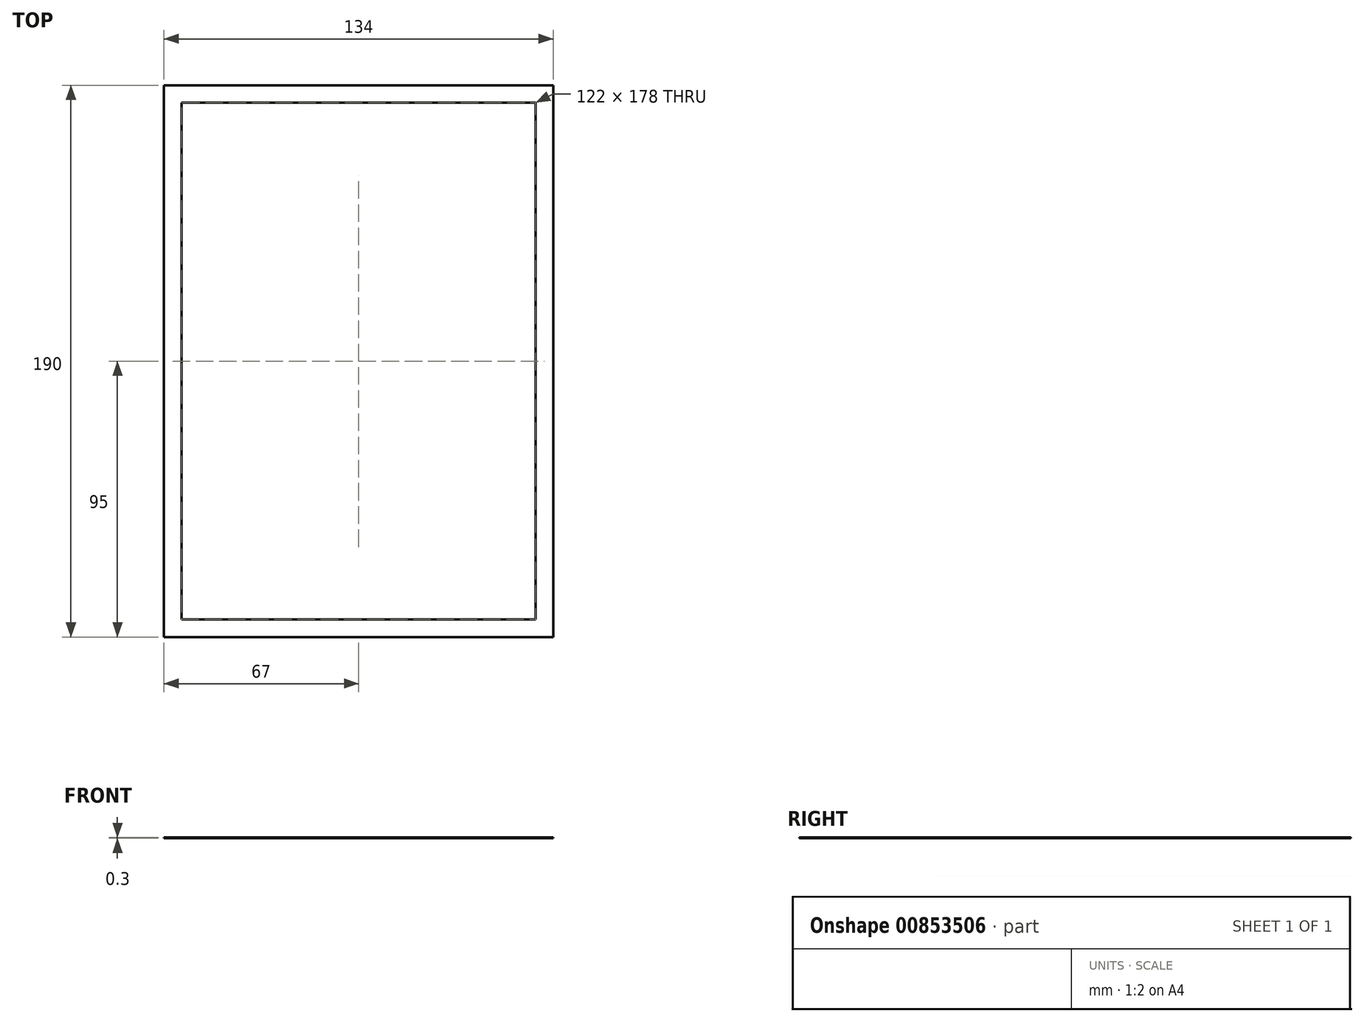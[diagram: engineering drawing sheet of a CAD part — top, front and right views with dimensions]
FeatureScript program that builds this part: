
annotation { "Feature Type Name" : "Feature", "Feature Type Description" : "" }
export const myFeature = defineFeature(function(context is Context, id is Id, definition is map)
    precondition{}
    {
        {
            var Q0;
            Q0=qCreatedBy(makeId("Top.planeOp"),FACE);
            var sketch = newSketch(context, id + "F0", { "sketchPlane" : qUnion([Q0])});
            skLineSegment(sketch, "E0.bottom", {"start": v(-67, 95) * mm, "end": v(67, 95) * mm});
            skLineSegment(sketch, "E0.top", {"start": v(-67, -95) * mm, "end": v(67, -95) * mm});
            skLineSegment(sketch, "E0.left", {"start": v(-67, 95) * mm, "end": v(-67, -95) * mm});
            skLineSegment(sketch, "E0.right", {"start": v(67, 95) * mm, "end": v(67, -95) * mm});
            skPoint(sketch, "E0.middle", {"position": v(0, 0) * mm});
            skLineSegment(sketch, "E1.0", {"start": v(-61, 89) * mm, "end": v(61, 89) * mm});
            skLineSegment(sketch, "E1.1", {"start": v(-61, 89) * mm, "end": v(-61, -89) * mm});
            skLineSegment(sketch, "E1.2", {"start": v(-61, -89) * mm, "end": v(61, -89) * mm});
            skLineSegment(sketch, "E1.3", {"start": v(61, 89) * mm, "end": v(61, -89) * mm});
            skSolve(sketch);
        }
        {
            var Q0;
            Q0 = qSketchRegion(id + "F0", true);
            extrude(context, id + "F1", {"entities" : qUnion([Q0]), "depth" : 0.3 * mm, "offsetDistance" : 25 * mm});
        }
    });
